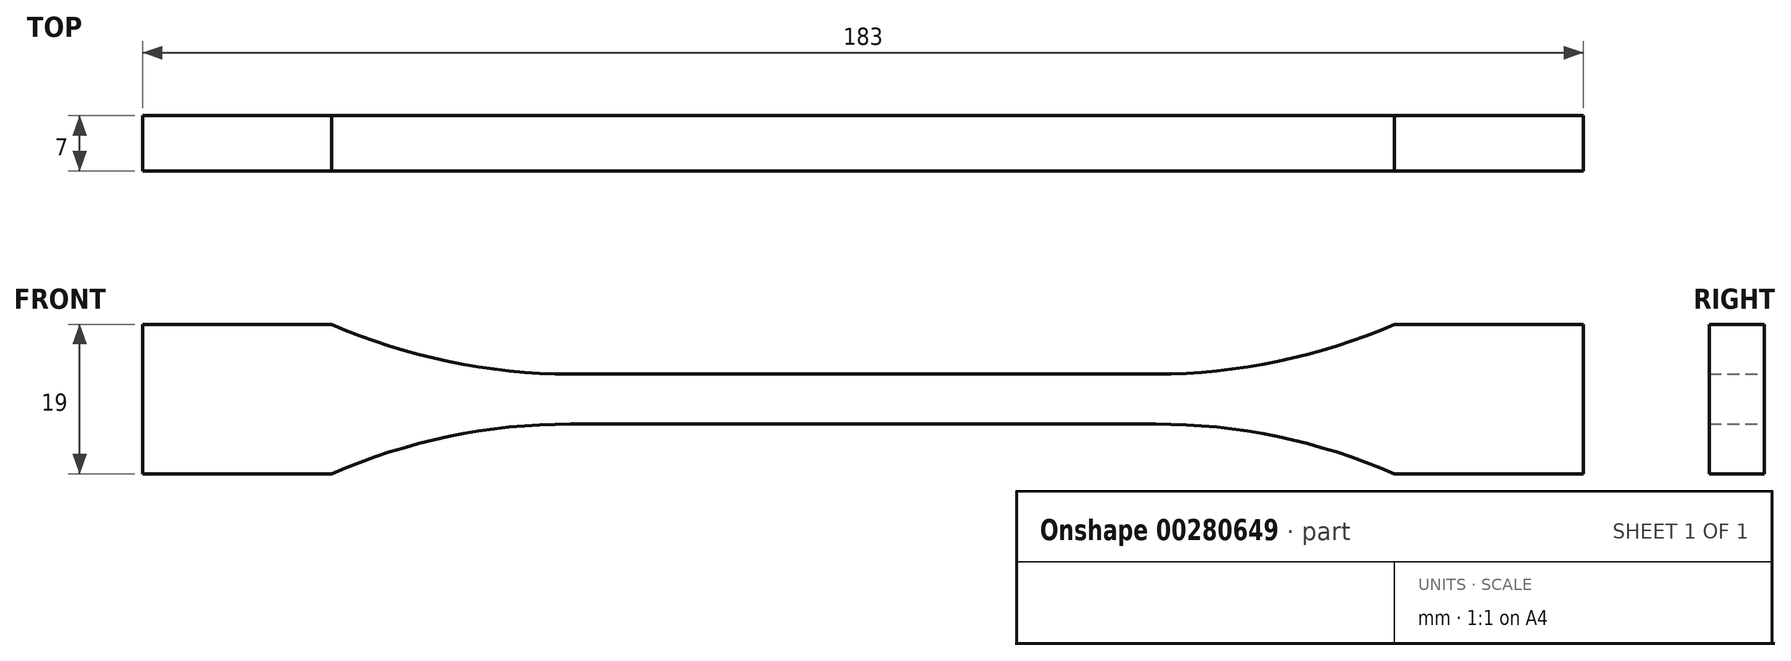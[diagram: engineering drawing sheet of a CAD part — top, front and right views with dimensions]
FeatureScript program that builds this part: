
annotation { "Feature Type Name" : "Feature", "Feature Type Description" : "" }
export const myFeature = defineFeature(function(context is Context, id is Id, definition is map)
    precondition{}
    {
        {
            var Q0;
            Q0=qCreatedBy(makeId("Front.planeOp"),FACE);
            var sketch = newSketch(context, id + "F0", { "sketchPlane" : qUnion([Q0])});
            skLineSegment(sketch, "E0", {"start": v(0, 3.17) * mm, "end": v(37.15, 3.17) * mm});
            skArc(sketch, "E1", {"start": v(37.15, 3.17) * mm, "mid": v(52.65, 4.77) * mm, "end": v(67.5, 9.5) * mm});
            skLineSegment(sketch, "E2", {"start": v(67.5, 9.5) * mm, "end": v(91.5, 9.5) * mm});
            skLineSegment(sketch, "E3.MirrorCS", {"start": v(0, -3.17) * mm, "end": v(37.15, -3.17) * mm});
            skLineSegment(sketch, "E4.MirrorCS", {"start": v(67.5, -9.5) * mm, "end": v(91.5, -9.5) * mm});
            skArc(sketch, "E5.MirrorCS", {"start": v(37.15, -3.17) * mm, "mid": v(52.65, -4.77) * mm, "end": v(67.5, -9.5) * mm});
            skLineSegment(sketch, "E6.MirrorCS", {"start": v(-67.5, 9.5) * mm, "end": v(-91.5, 9.5) * mm});
            skLineSegment(sketch, "E7.MirrorCS", {"start": v(-67.5, -9.5) * mm, "end": v(-91.5, -9.5) * mm});
            skArc(sketch, "E8.MirrorCS", {"start": v(-37.15, -3.17) * mm, "mid": v(-52.65, -4.77) * mm, "end": v(-67.5, -9.5) * mm});
            skLineSegment(sketch, "E9.MirrorCS", {"start": v(0, -3.18) * mm, "end": v(-37.15, -3.18) * mm});
            skLineSegment(sketch, "E10.MirrorCS", {"start": v(0, 3.17) * mm, "end": v(-37.15, 3.17) * mm});
            skArc(sketch, "E11.MirrorCS", {"start": v(-37.15, 3.17) * mm, "mid": v(-52.65, 4.77) * mm, "end": v(-67.5, 9.5) * mm});
            skLineSegment(sketch, "E12", {"start": v(-91.5, 9.5) * mm, "end": v(-91.5, -9.5) * mm});
            skLineSegment(sketch, "E13", {"start": v(91.5, 9.5) * mm, "end": v(91.5, -9.5) * mm});
            skSolve(sketch);
        }
        {
            var Q0;
            Q0 = qSketchRegion(id + "F0", true);
            extrude(context, id + "F1", {"entities" : qUnion([Q0]), "depth" : 7 * mm});
        }
    });
